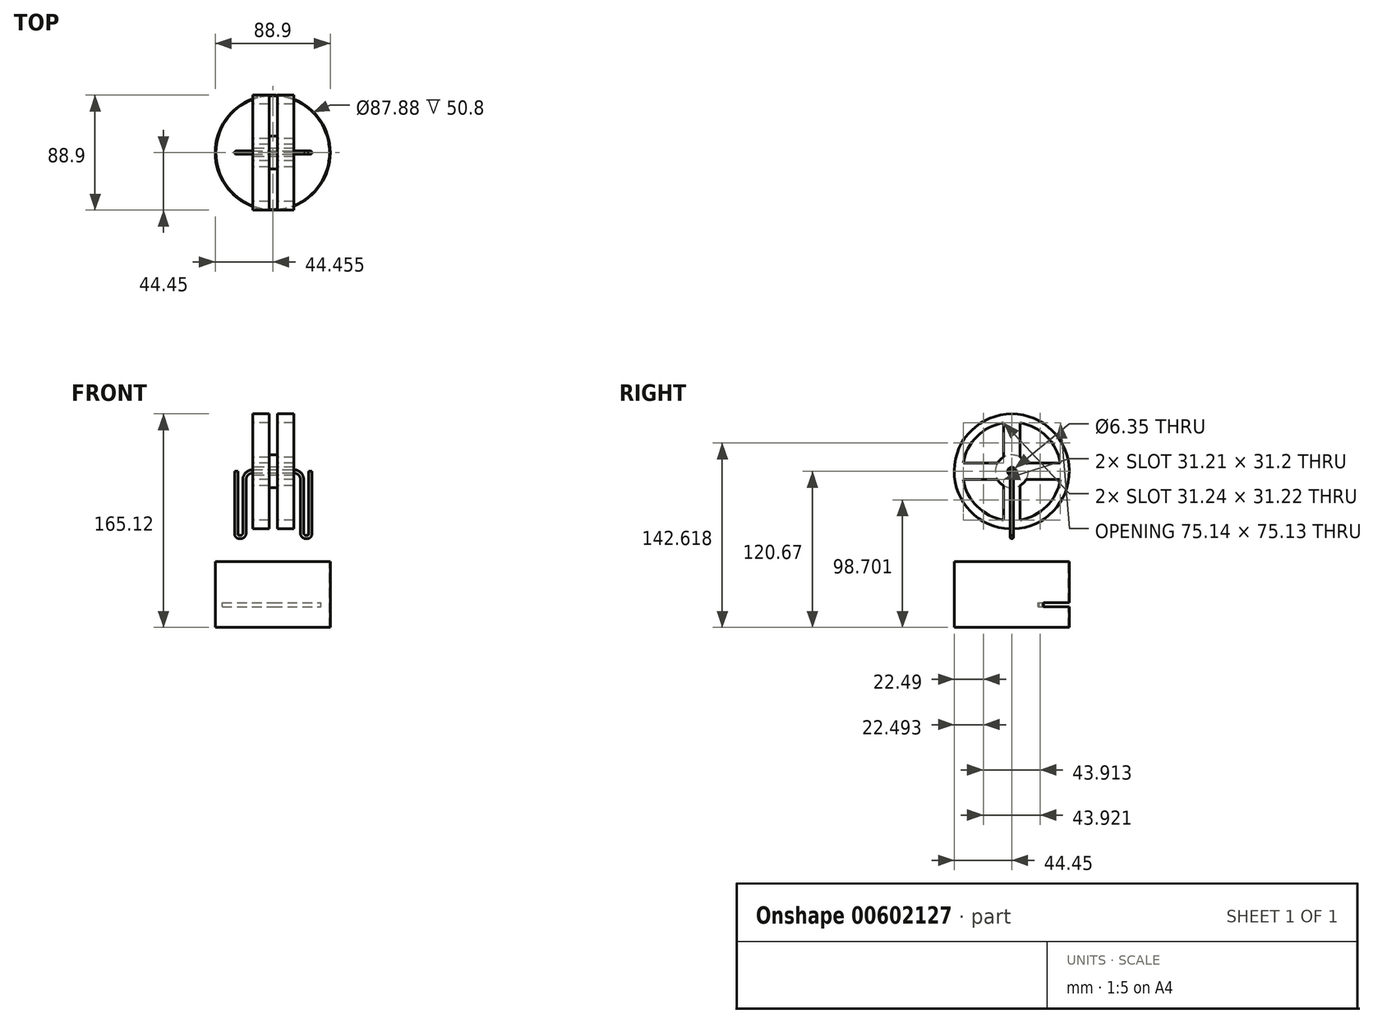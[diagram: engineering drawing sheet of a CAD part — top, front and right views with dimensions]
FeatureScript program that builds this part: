
annotation { "Feature Type Name" : "Feature", "Feature Type Description" : "" }
export const myFeature = defineFeature(function(context is Context, id is Id, definition is map)
    precondition{}
    {
        {
            var Q0;
            Q0=qCreatedBy(makeId("Right.planeOp"),FACE);
            var sketch = newSketch(context, id + "F0", { "sketchPlane" : qUnion([Q0])});
            skCircle(sketch, "E0", {"center": v(0, 0) * mm, "radius": 38.1 * mm});
            skCircle(sketch, "E1", {"center": v(0, 0) * mm, "radius": 12.7 * mm});
            skLineSegment(sketch, "E2", {"start": v(11.01, 6.33) * mm, "end": v(37.57, 6.33) * mm});
            skLineSegment(sketch, "E3", {"start": v(10.99, -6.37) * mm, "end": v(37.56, -6.37) * mm});
            skLineSegment(sketch, "E4", {"start": v(-6.35, -11) * mm, "end": v(-6.35, -37.57) * mm});
            skLineSegment(sketch, "E5", {"start": v(6.35, -11) * mm, "end": v(6.35, -37.57) * mm});
            skCircle(sketch, "E6", {"center": v(0, 0) * mm, "radius": 44.45 * mm});
            skLineSegment(sketch, "E7", {"start": v(-10.99, -6.37) * mm, "end": v(-37.56, -6.37) * mm});
            skLineSegment(sketch, "E8", {"start": v(6.35, -12) * mm, "end": v(6.35, -11) * mm});
            skLineSegment(sketch, "E9.trimOffspring", {"start": v(-6.35, 11) * mm, "end": v(-6.35, 37.57) * mm});
            skLineSegment(sketch, "E10.trimOffspring", {"start": v(-11.01, 6.33) * mm, "end": v(-37.57, 6.33) * mm});
            skLineSegment(sketch, "E11.trimOffspring", {"start": v(6.35, 11) * mm, "end": v(6.35, 37.57) * mm});
            skCircle(sketch, "E12", {"center": v(0, 0) * mm, "radius": 3.18 * mm});
            skSolve(sketch);
        }
        {
            var Q0;
            Q0=makeQuery(id+"F0.imprint","IMPRINT",FACE,{"disambiguationData":[TD([[makeQuery(id+"F0.imprint","IMPRINT",EDGE,{"derivedFrom":sQuery(id+"F0.wireOp",EDGE,"E6")}),1.0]])]});
            var Q1;
            {var subQ0=sQuery(id+"F0.wireOp",EDGE,"E9.trimOffspring");Q1=makeQuery(id+"F0.imprint","IMPRINT",FACE,{"disambiguationData":[TD([[makeQuery(id+"F0.imprint","IMPRINT",EDGE,{"derivedFrom":subQ0}),-1.0]])]});}
            var Q2;
            {var subQ0=sQuery(id+"F0.wireOp",EDGE,"E7");Q2=makeQuery(id+"F0.imprint","IMPRINT",FACE,{"disambiguationData":[TD([[makeQuery(id+"F0.imprint","IMPRINT",EDGE,{"derivedFrom":subQ0}),-1.0]])]});}
            var Q3;
            {var subQ0=sQuery(id+"F0.wireOp",EDGE,"E2");Q3=makeQuery(id+"F0.imprint","IMPRINT",FACE,{"disambiguationData":[TD([[makeQuery(id+"F0.imprint","IMPRINT",EDGE,{"derivedFrom":subQ0}),-1.0]])]});}
            var Q4;
            {var subQ1=sQuery(id+"F0.wireOp",EDGE,"E4");Q4=makeQuery(id+"F0.imprint","IMPRINT",FACE,{"disambiguationData":[TD([[makeQuery(id+"F0.imprint","IMPRINT",EDGE,{"derivedFrom":subQ1}),1.0]])]});}
            var Q5;
            Q5=makeQuery(id+"F0.imprint","IMPRINT",FACE,{"disambiguationData":[TD([[makeQuery(id+"F0.imprint","IMPRINT",EDGE,{"derivedFrom":sQuery(id+"F0.wireOp",EDGE,"E12")}),-1.0]])]});
            extrude(context, id + "F1", {"entities" : qUnion([Q0, Q1, Q2, Q3, Q4, Q5]), "depth" : 12.7 * mm, "offsetDistance" : 25.4 * mm});
        }
        {
            var Q0;
            Q0=makeQuery(id+"F1.opExtrude","CAP_FACE",FACE,{"disambiguationData":[OSD([sQuery(id+"F0.wireOp",EDGE,"E0"),sQuery(id+"F0.wireOp",EDGE,"E1"),sQuery(id+"F0.wireOp",EDGE,"E2"),sQuery(id+"F0.wireOp",EDGE,"E3"),sQuery(id+"F0.wireOp",EDGE,"E4"),sQuery(id+"F0.wireOp",EDGE,"E5"),sQuery(id+"F0.wireOp",EDGE,"E6"),sQuery(id+"F0.wireOp",EDGE,"E7"),sQuery(id+"F0.wireOp",EDGE,"E8"),sQuery(id+"F0.wireOp",EDGE,"E9.trimOffspring"),sQuery(id+"F0.wireOp",EDGE,"E10.trimOffspring"),sQuery(id+"F0.wireOp",EDGE,"E11.trimOffspring"),sQuery(id+"F0.wireOp",EDGE,"E12")])],"isStart":false});
            var sketch = newSketch(context, id + "F2", { "sketchPlane" : qUnion([Q0])});
            skCircle(sketch, "E13", {"center": v(0, 0) * mm, "radius": 12.7 * mm});
            skCircle(sketch, "E14", {"center": v(0, 0) * mm, "radius": 3.18 * mm});
            skSolve(sketch);
        }
        {
            var Q0;
            Q0=makeQuery(id+"F2.imprint","IMPRINT",FACE,{"disambiguationData":[TD([[makeQuery(id+"F2.imprint","IMPRINT",EDGE,{"derivedFrom":sQuery(id+"F2.wireOp",EDGE,"E14")}),-1.0]])]});
            extrude(context, id + "F3", {"entities" : qUnion([Q0]), "operationType" : NewBodyOperationType.ADD, "depth" : 6.35 * mm, "offsetDistance" : 25.4 * mm});
        }
        {
            var Q0;
            Q0=makeQuery(id+"F3.opExtrude","CAP_FACE",FACE,{"disambiguationData":[OSD([sQuery(id+"F2.wireOp",EDGE,"E13"),sQuery(id+"F2.wireOp",EDGE,"E14")])],"isStart":false});
            var sketch = newSketch(context, id + "F4", { "sketchPlane" : qUnion([Q0])});
            skCircle(sketch, "E15", {"center": v(0, 0) * mm, "radius": 38.1 * mm});
            skCircle(sketch, "E16", {"center": v(0, 0) * mm, "radius": 12.7 * mm});
            skCircle(sketch, "E17", {"center": v(0, 0) * mm, "radius": 44.45 * mm});
            skLineSegment(sketch, "E18", {"start": v(-6.35, 37.57) * mm, "end": v(-6.35, 11) * mm});
            skLineSegment(sketch, "E19", {"start": v(6.35, 37.57) * mm, "end": v(6.35, 11) * mm});
            skLineSegment(sketch, "E20", {"start": v(21.12, 6.35) * mm, "end": v(37.57, 6.35) * mm});
            skLineSegment(sketch, "E21", {"start": v(21.12, -6.35) * mm, "end": v(37.57, -6.35) * mm});
            skLineSegment(sketch, "E22", {"start": v(21.12, 6.35) * mm, "end": v(11, 6.35) * mm});
            skLineSegment(sketch, "E23", {"start": v(21.12, -6.35) * mm, "end": v(11, -6.35) * mm});
            skLineSegment(sketch, "E24.trimOffspring", {"start": v(-11, 6.35) * mm, "end": v(-37.57, 6.35) * mm});
            skLineSegment(sketch, "E25.trimOffspring", {"start": v(-6.35, -11) * mm, "end": v(-6.35, -37.57) * mm});
            skLineSegment(sketch, "E26.trimOffspring", {"start": v(-11, -6.35) * mm, "end": v(-37.57, -6.35) * mm});
            skLineSegment(sketch, "E27.trimOffspring", {"start": v(6.35, -11) * mm, "end": v(6.35, -37.57) * mm});
            skSolve(sketch);
        }
        {
            var Q0;
            {var subQ0=sQuery(id+"F4.wireOp",EDGE,"E18");Q0=makeQuery(id+"F4.imprint","IMPRINT",FACE,{"disambiguationData":[TD([[makeQuery(id+"F4.imprint","IMPRINT",EDGE,{"derivedFrom":subQ0}),1.0]])]});}
            var Q1;
            {var subQ0=sQuery(id+"F4.wireOp",EDGE,"E20");Q1=makeQuery(id+"F4.imprint","IMPRINT",FACE,{"disambiguationData":[TD([[makeQuery(id+"F4.imprint","IMPRINT",EDGE,{"derivedFrom":subQ0}),-1.0]])]});}
            var Q2;
            {var subQ0=sQuery(id+"F4.wireOp",EDGE,"E25.trimOffspring");Q2=makeQuery(id+"F4.imprint","IMPRINT",FACE,{"disambiguationData":[TD([[makeQuery(id+"F4.imprint","IMPRINT",EDGE,{"derivedFrom":subQ0}),1.0]])]});}
            var Q3;
            {var subQ0=sQuery(id+"F4.wireOp",EDGE,"E24.trimOffspring");Q3=makeQuery(id+"F4.imprint","IMPRINT",FACE,{"disambiguationData":[TD([[makeQuery(id+"F4.imprint","IMPRINT",EDGE,{"derivedFrom":subQ0}),1.0]])]});}
            var Q4;
            Q4=makeQuery(id+"F4.imprint","IMPRINT",FACE,{"disambiguationData":[TD([[makeQuery(id+"F4.imprint","IMPRINT",EDGE,{"derivedFrom":makeQuery(id+"F3.opExtrude","CAP_EDGE",EDGE,{"disambiguationData":[OSD([sQuery(id+"F2.wireOp",EDGE,"E14")])],"isStart":false})}),-1.0]])]});
            var Q5;
            Q5=makeQuery(id+"F4.imprint","IMPRINT",FACE,{"disambiguationData":[TD([[makeQuery(id+"F4.imprint","IMPRINT",EDGE,{"derivedFrom":sQuery(id+"F4.wireOp",EDGE,"E17")}),1.0]])]});
            extrude(context, id + "F5", {"entities" : qUnion([Q0, Q1, Q2, Q3, Q4, Q5]), "operationType" : NewBodyOperationType.ADD, "depth" : 12.7 * mm, "offsetDistance" : 25.4 * mm});
        }
        {
            var Q0;
            Q0=makeQuery(id+"F5.opExtrude","CAP_FACE",FACE,{"disambiguationData":[OSD([sQuery(id+"F2.wireOp",EDGE,"E14"),sQuery(id+"F4.wireOp",EDGE,"E15"),sQuery(id+"F4.wireOp",EDGE,"E16"),sQuery(id+"F4.wireOp",EDGE,"E17"),sQuery(id+"F4.wireOp",EDGE,"E18"),sQuery(id+"F4.wireOp",EDGE,"E19"),sQuery(id+"F4.wireOp",EDGE,"E20"),sQuery(id+"F4.wireOp",EDGE,"E21"),sQuery(id+"F4.wireOp",EDGE,"E22"),sQuery(id+"F4.wireOp",EDGE,"E23"),sQuery(id+"F4.wireOp",EDGE,"E24.trimOffspring"),sQuery(id+"F4.wireOp",EDGE,"E25.trimOffspring"),sQuery(id+"F4.wireOp",EDGE,"E26.trimOffspring"),sQuery(id+"F4.wireOp",EDGE,"E27.trimOffspring")])],"isStart":false});
            var sketch = newSketch(context, id + "F6", { "sketchPlane" : qUnion([Q0])});
            skCircle(sketch, "E28", {"center": v(0, 0) * mm, "radius": 1.02 * mm});
            skSolve(sketch);
        }
        {
            var Q0;
            Q0=makeQuery(id+"F6.imprint","IMPRINT",FACE,{"disambiguationData":[TD([[makeQuery(id+"F6.imprint","IMPRINT",EDGE,{"derivedFrom":sQuery(id+"F6.wireOp",EDGE,"E28")}),1.0]])]});
            extrude(context, id + "F7", {"entities" : qUnion([Q0]), "depth" : 25.4 * mm, "offsetDistance" : 25.4 * mm});
        }
        {
            var Q0;
            Q0=makeQuery(id+"F7.opExtrude","CAP_FACE",FACE,{"disambiguationData":[OSD([sQuery(id+"F6.wireOp",EDGE,"E28")])],"isStart":true});
            var sketch = newSketch(context, id + "F8", { "sketchPlane" : qUnion([Q0])});
            skCircle(sketch, "E29", {"center": v(0, 0) * mm, "radius": 10.23 * mm});
            skCircle(sketch, "E30", {"center": v(0, 0) * mm, "radius": 1.02 * mm});
            skSolve(sketch);
        }
        {
            var Q0;
            Q0=makeQuery(id+"F8.imprint","IMPRINT",FACE,{"disambiguationData":[TD([[makeQuery(id+"F8.imprint","IMPRINT",EDGE,{"derivedFrom":sQuery(id+"F8.wireOp",EDGE,"E30")}),-1.0]])]});
            extrude(context, id + "F9", {"entities" : qUnion([Q0]), "operationType" : NewBodyOperationType.ADD, "depth" : 55.88 * mm, "offsetDistance" : 25.4 * mm});
        }
        {
            var Q0;
            Q0=makeQuery(id+"F7.opExtrude","SWEPT_BODY",BODY,{"disambiguationData":[OSD([sQuery(id+"F6.wireOp",EDGE,"E28")])]});
            deleteBodies(context, id + "F10", {"entities" : qUnion([Q0])});
        }
        {
            var Q0;
            Q0=qCreatedBy(makeId("Front.planeOp"),FACE);
            var sketch = newSketch(context, id + "F11", { "sketchPlane" : qUnion([Q0])});
            skLineSegment(sketch, "E31", {"start": v(38.1, -6.35) * mm, "end": v(38.1, -47.62) * mm});
            skLineSegment(sketch, "E32", {"start": v(-9.52, -50.8) * mm, "end": v(-10.32, -50.8) * mm});
            skLineSegment(sketch, "E33", {"start": v(41.28, -50.8) * mm, "end": v(42.07, -50.8) * mm});
            skLineSegment(sketch, "E34", {"start": v(-12.7, -48.42) * mm, "end": v(-12.7, 0) * mm});
            skLineSegment(sketch, "E35", {"start": v(44.45, -48.42) * mm, "end": v(44.45, 0) * mm});
            skLineSegment(sketch, "E36", {"start": v(-6.35, -47.63) * mm, "end": v(-6.35, -6.35) * mm});
            skLineSegment(sketch, "E37", {"start": v(0, 0) * mm, "end": v(31.75, 0) * mm});
            skPoint(sketch, "E38.visualSharp", {"position": v(-6.35, 0) * mm});
            skArc(sketch, "E38.filletArc", {"start": v(0, 0) * mm, "mid": v(-4.5, -1.86) * mm, "end": v(-6.35, -6.35) * mm});
            skPoint(sketch, "E39.visualSharp", {"position": v(38.1, 0) * mm});
            skArc(sketch, "E39.filletArc", {"start": v(38.1, -6.35) * mm, "mid": v(36.24, -1.86) * mm, "end": v(31.75, 0) * mm});
            skPoint(sketch, "E40.visualSharp", {"position": v(-6.35, -50.8) * mm});
            skArc(sketch, "E40.filletArc", {"start": v(-9.52, -50.8) * mm, "mid": v(-7.28, -49.87) * mm, "end": v(-6.35, -47.63) * mm});
            skPoint(sketch, "E41.visualSharp", {"position": v(38.1, -50.8) * mm});
            skArc(sketch, "E41.filletArc", {"start": v(38.1, -47.62) * mm, "mid": v(39.03, -49.87) * mm, "end": v(41.28, -50.8) * mm});
            skPoint(sketch, "E42.visualSharp", {"position": v(-12.7, -50.8) * mm});
            skArc(sketch, "E42.filletArc", {"start": v(-12.7, -48.42) * mm, "mid": v(-12, -50.1) * mm, "end": v(-10.32, -50.8) * mm});
            skPoint(sketch, "E43.visualSharp", {"position": v(44.45, -50.8) * mm});
            skArc(sketch, "E43.filletArc", {"start": v(42.07, -50.8) * mm, "mid": v(43.75, -50.1) * mm, "end": v(44.45, -48.42) * mm});
            skSolve(sketch);
        }
        {
            var Q0;
            Q0=qCreatedBy(makeId("Top.planeOp"),FACE);
            var sketch = newSketch(context, id + "F12", { "sketchPlane" : qUnion([Q0])});
            skPoint(sketch, "E44.0", {"position": v(-12.7, 0) * mm});
            skCircle(sketch, "E45", {"center": v(-12.7, 0) * mm, "radius": 1.27 * mm});
            skSolve(sketch);
        }
        {
            var Q0;
            Q0=makeQuery(id+"F12.imprint","IMPRINT",FACE,{"disambiguationData":[TD([[makeQuery(id+"F12.imprint","IMPRINT",EDGE,{"derivedFrom":sQuery(id+"F12.wireOp",EDGE,"E45")}),1.0]])]});
            var Q1;
            Q1=sQuery(id+"F11.wireOp",EDGE,"E34");
            var Q2;
            Q2=sQuery(id+"F11.wireOp",EDGE,"E42.filletArc");
            var Q3;
            Q3=sQuery(id+"F11.wireOp",EDGE,"E40.filletArc");
            var Q4;
            Q4=sQuery(id+"F11.wireOp",EDGE,"E36");
            var Q5;
            Q5=sQuery(id+"F11.wireOp",EDGE,"E32");
            var Q6;
            Q6=sQuery(id+"F11.wireOp",EDGE,"E38.filletArc");
            var Q7;
            Q7=sQuery(id+"F11.wireOp",EDGE,"E37");
            var Q8;
            Q8=sQuery(id+"F11.wireOp",EDGE,"E39.filletArc");
            var Q9;
            Q9=sQuery(id+"F11.wireOp",EDGE,"E31");
            var Q10;
            Q10=sQuery(id+"F11.wireOp",EDGE,"E41.filletArc");
            var Q11;
            Q11=sQuery(id+"F11.wireOp",EDGE,"E33");
            var Q12;
            Q12=sQuery(id+"F11.wireOp",EDGE,"E43.filletArc");
            var Q13;
            Q13=sQuery(id+"F11.wireOp",EDGE,"E35");
            sweep(context, id + "F13", {"profiles" : qUnion([Q0]), "path" : qUnion([Q1, Q2, Q3, Q4, Q5, Q6, Q7, Q8, Q9, Q10, Q11, Q12, Q13])});
        }
        {
            var Q0;
            Q0=makeQuery(id+"F1.opExtrude","SWEPT_FACE",FACE,{"disambiguationData":[OSD([sQuery(id+"F0.wireOp",EDGE,"E7")])]});
            cPlane(context, id + "F14", {"entities" : qUnion([Q0]), "cplaneType" : CPlaneType.OFFSET, "offset" : 63.5 * mm, "width" : 152.4 * mm, "height" : 152.4 * mm});
        }
        {
            var Q0;
            Q0=qCreatedBy(id+"F14.planeOp",FACE);
            var sketch = newSketch(context, id + "F15", { "sketchPlane" : qUnion([Q0])});
            skCircle(sketch, "E46", {"center": v(15.46, 0) * mm, "radius": 44.45 * mm});
            skCircle(sketch, "E47", {"center": v(15.46, 0) * mm, "radius": 43.94 * mm});
            skSolve(sketch);
        }
        {
            var Q0;
            Q0=makeQuery(id+"F15.imprint","IMPRINT",FACE,{"disambiguationData":[TD([[makeQuery(id+"F15.imprint","IMPRINT",EDGE,{"derivedFrom":sQuery(id+"F15.wireOp",EDGE,"E46")}),1.0]])]});
            extrude(context, id + "F16", {"entities" : qUnion([Q0]), "depth" : 50.8 * mm, "offsetDistance" : 25.4 * mm});
        }
        {
            var Q0;
            Q0=qCreatedBy(makeId("Front.planeOp"),FACE);
            cPlane(context, id + "F17", {"entities" : qUnion([Q0]), "cplaneType" : CPlaneType.OFFSET, "offset" : 63.5 * mm, "oppositeDirection" : true, "width" : 152.4 * mm, "height" : 152.4 * mm});
        }
        {
            var Q0;
            Q0=qCreatedBy(id+"F17.planeOp",FACE);
            var sketch = newSketch(context, id + "F18", { "sketchPlane" : qUnion([Q0])});
            skLineSegment(sketch, "E48", {"start": v(52.65, -101.62) * mm, "end": v(-23.55, -101.62) * mm});
            skLineSegment(sketch, "E49", {"start": v(52.65, -101.62) * mm, "end": v(52.65, -104.7) * mm});
            skLineSegment(sketch, "E50", {"start": v(52.65, -104.7) * mm, "end": v(-23.55, -104.7) * mm});
            skLineSegment(sketch, "E51", {"start": v(-23.55, -104.7) * mm, "end": v(-23.55, -101.62) * mm});
            skSolve(sketch);
        }
        {
            var Q0;
            Q0=makeQuery(id+"F18.imprint","IMPRINT",FACE,{"disambiguationData":[TD([[makeQuery(id+"F18.imprint","IMPRINT",EDGE,{"derivedFrom":sQuery(id+"F18.wireOp",EDGE,"E48")}),1.0]])]});
            extrude(context, id + "F19", {"entities" : qUnion([Q0]), "operationType" : NewBodyOperationType.REMOVE, "depth" : 50.8 * mm, "offsetDistance" : 25.4 * mm});
        }
    });
